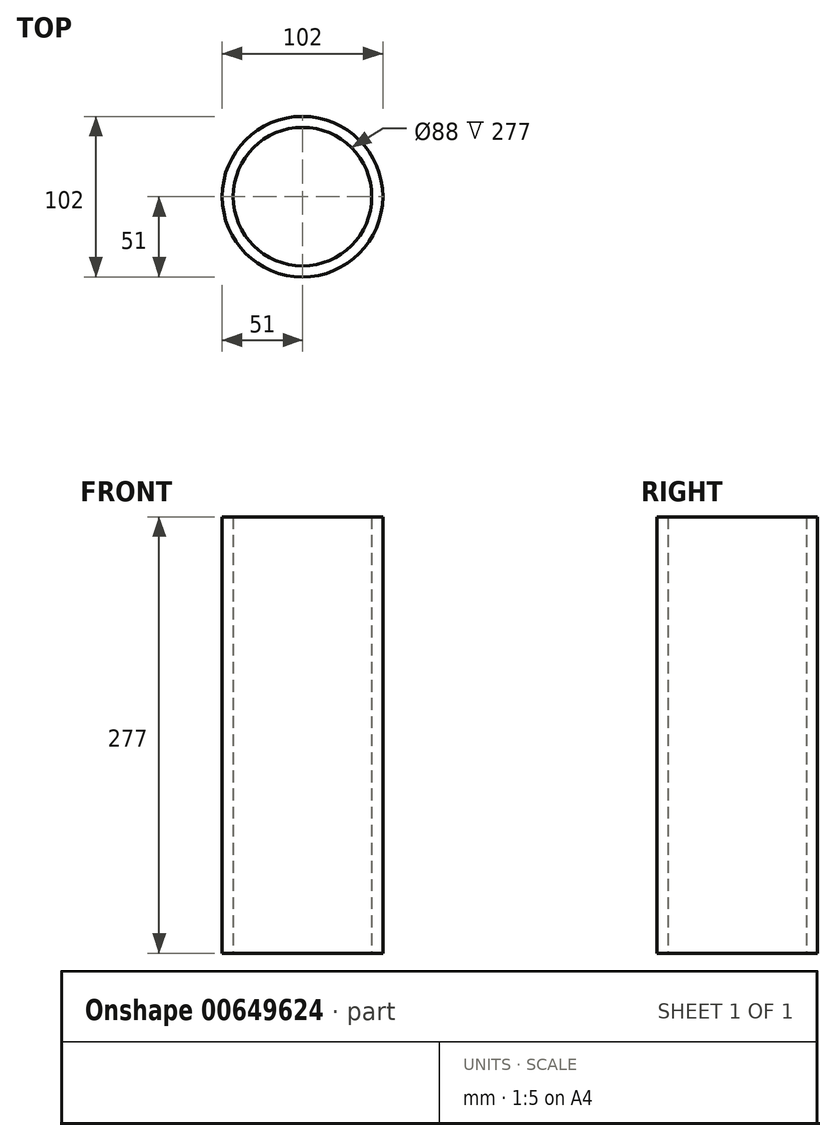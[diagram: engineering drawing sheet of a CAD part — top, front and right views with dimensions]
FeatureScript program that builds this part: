
annotation { "Feature Type Name" : "Feature", "Feature Type Description" : "" }
export const myFeature = defineFeature(function(context is Context, id is Id, definition is map)
    precondition{}
    {
        {
            var Q0;
            Q0=qCreatedBy(makeId("Top.planeOp"),FACE);
            var sketch = newSketch(context, id + "F0", { "sketchPlane" : qUnion([Q0])});
            skCircle(sketch, "E0", {"center": v(0, 0) * mm, "radius": 51 * mm});
            skCircle(sketch, "E1", {"center": v(0, 0) * mm, "radius": 44 * mm});
            skSolve(sketch);
        }
        {
            var Q0;
            Q0=makeQuery(id+"F0.imprint","IMPRINT",FACE,{"disambiguationData":[TD([[makeQuery(id+"F0.imprint","IMPRINT",EDGE,{"derivedFrom":sQuery(id+"F0.wireOp",EDGE,"E0")}),1.0]])]});
            extrude(context, id + "F1", {"entities" : qUnion([Q0]), "depth" : 277 * mm, "offsetDistance" : 25 * mm});
        }
    });
